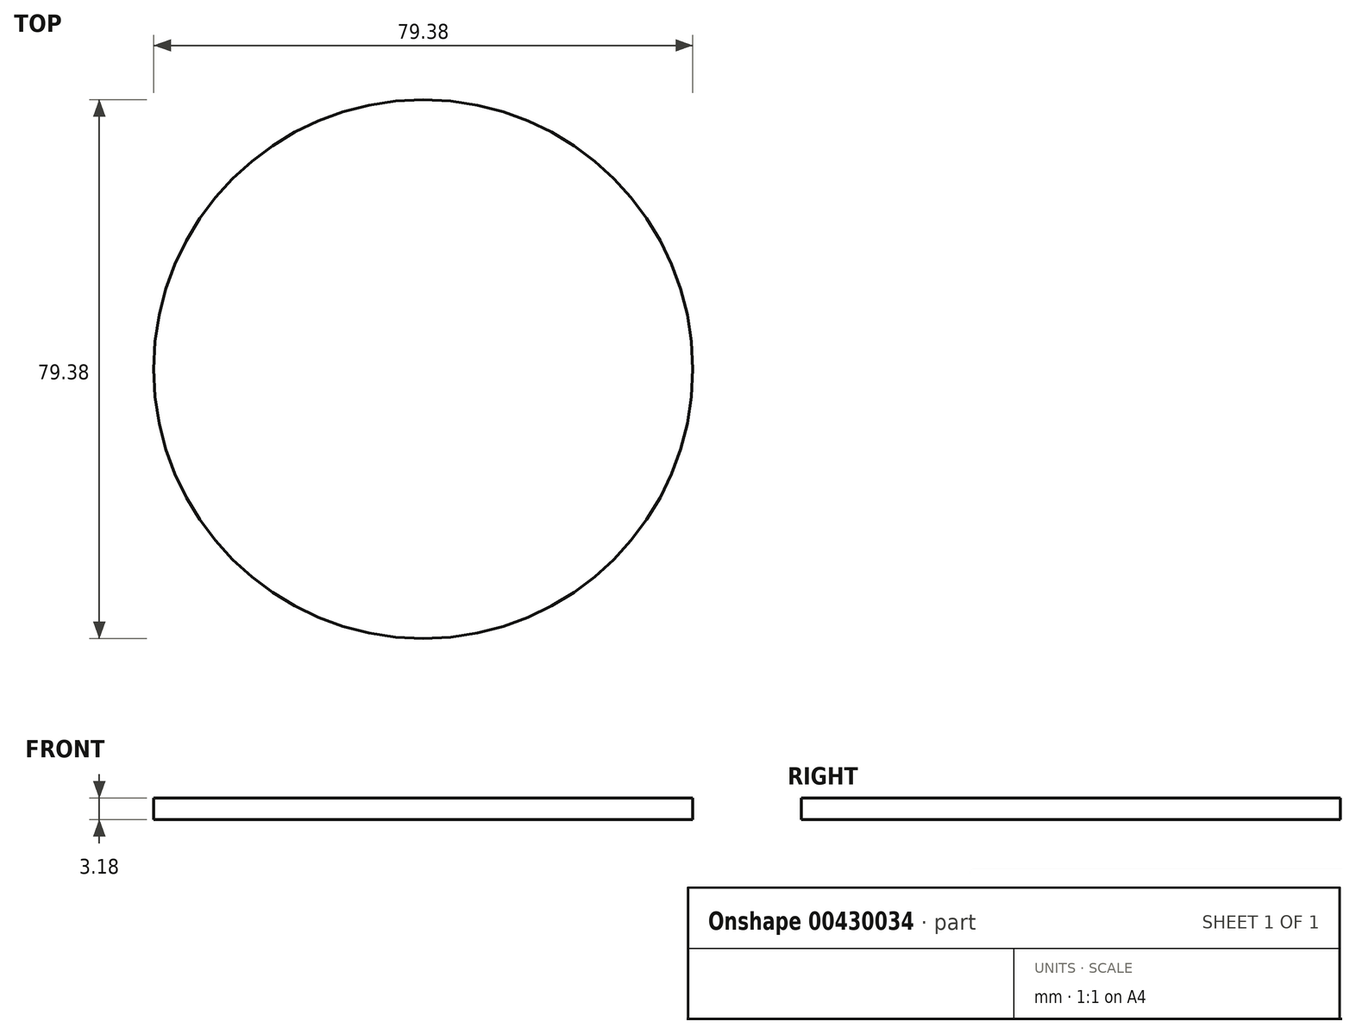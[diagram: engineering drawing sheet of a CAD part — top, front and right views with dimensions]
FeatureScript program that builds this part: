
annotation { "Feature Type Name" : "Feature", "Feature Type Description" : "" }
export const myFeature = defineFeature(function(context is Context, id is Id, definition is map)
    precondition{}
    {
        {
            var Q0;
            Q0=qCreatedBy(makeId("Top.planeOp"),FACE);
            var sketch = newSketch(context, id + "F0", { "sketchPlane" : qUnion([Q0])});
            skCircle(sketch, "E0", {"center": v(0, 0) * mm, "radius": 39.69 * mm});
            skSolve(sketch);
        }
        {
            var Q0;
            Q0 = qSketchRegion(id + "F0", true);
            extrude(context, id + "F1", {"entities" : qUnion([Q0]), "depth" : 3.17 * mm});
        }
    });
